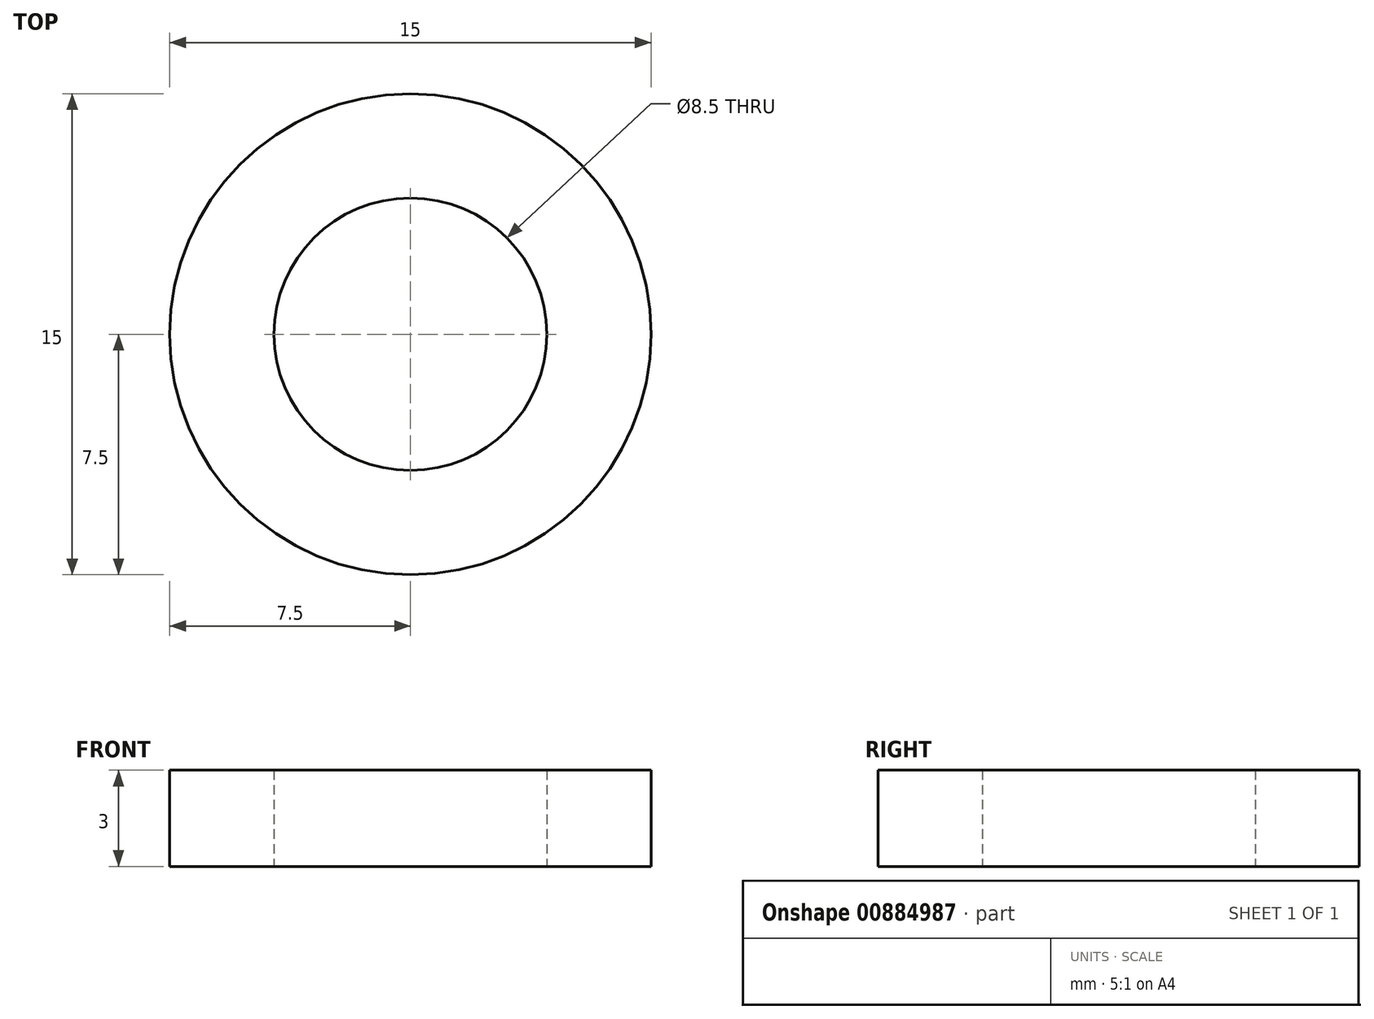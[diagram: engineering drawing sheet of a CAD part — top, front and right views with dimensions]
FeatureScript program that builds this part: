
annotation { "Feature Type Name" : "Feature", "Feature Type Description" : "" }
export const myFeature = defineFeature(function(context is Context, id is Id, definition is map)
    precondition{}
    {
        {
            var Q0;
            Q0=qCreatedBy(makeId("Top.planeOp"),FACE);
            var sketch = newSketch(context, id + "F0", { "sketchPlane" : qUnion([Q0])});
            skCircle(sketch, "E0", {"center": v(0, 0) * mm, "radius": 4.25 * mm});
            skCircle(sketch, "E1", {"center": v(0, 0) * mm, "radius": 7.5 * mm});
            skSolve(sketch);
        }
        {
            var Q0;
            Q0=makeQuery(id+"F0.imprint","IMPRINT",FACE,{"disambiguationData":[TD([[makeQuery(id+"F0.imprint","IMPRINT",EDGE,{"derivedFrom":sQuery(id+"F0.wireOp",EDGE,"E0")}),-1.0]])]});
            extrude(context, id + "F1", {"entities" : qUnion([Q0]), "depth" : 3 * mm, "offsetDistance" : 25 * mm});
        }
    });
